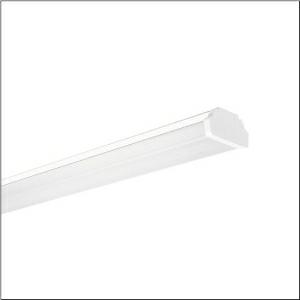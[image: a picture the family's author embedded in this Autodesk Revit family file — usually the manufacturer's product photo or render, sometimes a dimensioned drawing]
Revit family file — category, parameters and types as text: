
# Revit family: dus_31_gen_2_53bd812cv49xc2_ea29
name_source: partatom
category: Lighting Fixtures
units: mm (PartAtom-declared; Revit-internal decimal feet)

## family parameters
Cut with Voids When Loaded = No
Host = Face
Light Source = No
Part Type = Normal
Room Calculation Point = No
Round Connector Dimension = Use Diameter
Shared = No

## types (1)
- --- (1 x LED, 9240 lm, 49.9 W, 4000K)
    Apparent Load = 50 VA
    CIE Flux Codes = 47 80 95 93 100
    Color Rendering = 80
    Color Temperature = 4000K
    Default Elevation = 1800 mm
    Description = DUS 31 Gen.2, luminaire insert, of sheet steel, coil coated, white, length: 1.535mm, width: 81mm, height: 90mm, 5x system unit, system units: 307mm, LED rated luminous flux: 9.240lm, light colour: 840, SDCM (Standard Deviation of Colour Matching)MacAdam ≤ 3 SDCM (initial), control gear: ON/OFF Multilumen, CLOi, with plug, 3-pole, with phase selection, mains connection: 220..240V, AC, 50/60Hz, start of lifetime: 50W, end of service life: 61W, through-wiring accessed according to module size, primary optical cover: cover, of PMMA, light emission: direct distribution, primary light characteristic: symmetric, protection rating (complete): IP20, protection rating (LED compartment): IP50, insulation class (complete): insulation class I (protective earthing), certification: CE, ENEC, VDE, UKCA, impact resistance: IK03, permissible ambient temperature for indoor applications: -35..+40°C, corresponds to IFS (International Featured Standards) requirements for safety and quality in the food industry, reducing of maximum allowable ambient temperature of 5°C with ceiling mounting, packaging unit: 1 piece
    Height = 95 mm
    Lamp = 1 x LED
    Lamp Light Flux = 9240 lm
    Lamp Power = 49.9 W
    Lamp count = 1
    Length = 1535 mm
    Luminous efficacy = 185 lm/W
    Manufacturer = Siteco
    ModVariant = No
    Model = 53BD812CV49XC2
    Mounting Place = Ceiling
    Mounting Type = Pendant
    Number of Poles = 1
    OnlyDefault = Yes
    Power Factor = 1
    Product Name = DUS 31 Gen.2
    Product group = luminaire insert | ceiling pendant
    ProductGroupID = 901
    Protection Class = Protection class I
    Protection Degree = IP 20
    RLX_Detail_Level = 1
    RLX_Emergency_Light_Flux = 0 lm
    RLX_Emergency_Type = 0
    RLX_Emergency_Type_DB = No
    RlxData = <blob elided: 29869 chars, md5=fb588d6f>
    Socket = socket
    Standby Power = 0 W
    System Light Flux = 9240 lm
    System Power = 50 W
    Type Comments = factory setting: luminous flux: 100 % | (A | C | E) | 116 mA
    Type Image = l_1319596.jpg
    URL = http://relux.com
    VarID = @adj_049691
    Voltage = 0 V
    Weight = 0.00 kg
    Width = 81 mm

## geometry (parser evidence)
native form markers: Blend x4, Sweep x12
no freeform markers — native parametric forms only
